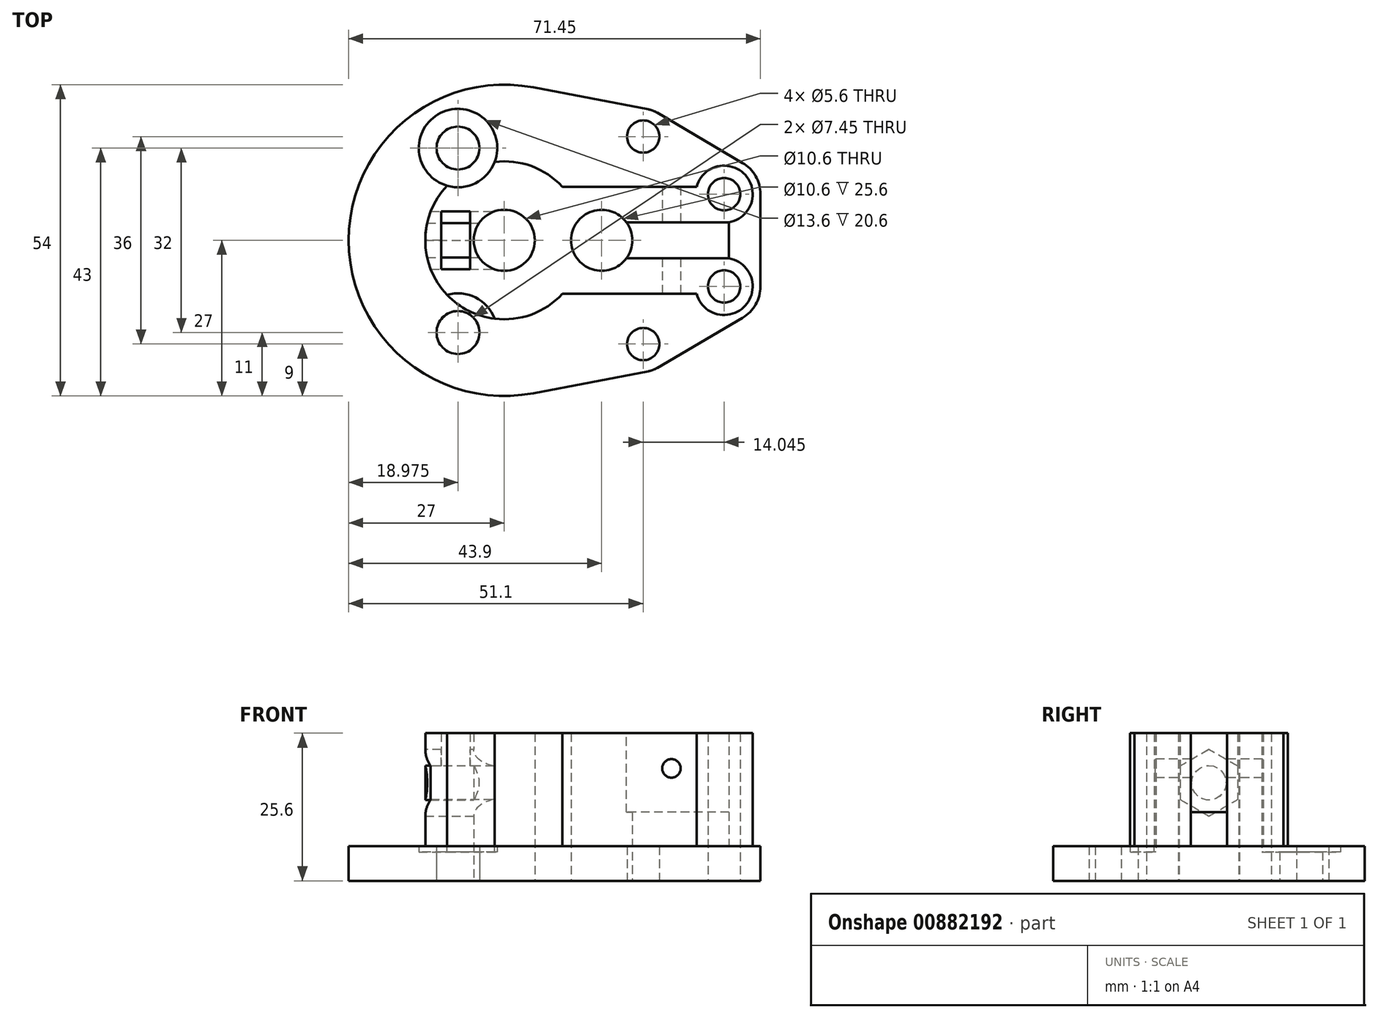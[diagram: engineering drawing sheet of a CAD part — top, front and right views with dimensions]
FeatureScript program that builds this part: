
annotation { "Feature Type Name" : "Feature", "Feature Type Description" : "" }
export const myFeature = defineFeature(function(context is Context, id is Id, definition is map)
    precondition{}
    {
        {
            var Q0;
            Q0=qCreatedBy(makeId("Top.planeOp"),FACE);
            var sketch = newSketch(context, id + "F0", { "sketchPlane" : qUnion([Q0])});
            skCircle(sketch, "E0", {"center": v(0, 0) * mm, "radius": 27 * mm, "construction": true});
            skCircle(sketch, "E1", {"center": v(0, 0) * mm, "radius": 5.3 * mm});
            skCircle(sketch, "E2", {"center": v(16.9, 0) * mm, "radius": 5.3 * mm});
            skCircle(sketch, "E3", {"center": v(-8.03, 16) * mm, "radius": 3.73 * mm});
            skCircle(sketch, "E4", {"center": v(24.1, 18) * mm, "radius": 2.8 * mm});
            skCircle(sketch, "E5", {"center": v(38.15, 8) * mm, "radius": 2.8 * mm});
            skCircle(sketch, "E6.MirrorC", {"center": v(-8.03, -16) * mm, "radius": 3.73 * mm});
            skCircle(sketch, "E7.MirrorC", {"center": v(24.1, -18) * mm, "radius": 2.8 * mm});
            skCircle(sketch, "E8.MirrorC", {"center": v(38.15, -8) * mm, "radius": 2.8 * mm});
            skCircle(sketch, "E9", {"center": v(24.1, 18) * mm, "radius": 4.8 * mm, "construction": true});
            skCircle(sketch, "E10", {"center": v(38.15, 8) * mm, "radius": 6.3 * mm, "construction": true});
            skLineSegment(sketch, "E11", {"start": v(26.53, 22.14) * mm, "end": v(41.34, 13.43) * mm});
            skCircle(sketch, "E12.MirrorC", {"center": v(38.15, -8) * mm, "radius": 6.3 * mm, "construction": true});
            skCircle(sketch, "E13.MirrorC", {"center": v(24.1, -18) * mm, "radius": 4.8 * mm, "construction": true});
            skLineSegment(sketch, "E14", {"start": v(44.45, 8) * mm, "end": v(44.45, -8) * mm});
            skLineSegment(sketch, "E15", {"start": v(41.34, -13.43) * mm, "end": v(26.53, -22.14) * mm});
            skLineSegment(sketch, "E16", {"start": v(5.06, 26.52) * mm, "end": v(25, 22.71) * mm});
            skLineSegment(sketch, "E17", {"start": v(5.06, -26.52) * mm, "end": v(25, -22.71) * mm});
            skArc(sketch, "E18", {"start": v(26.53, 22.14) * mm, "mid": v(25.8, 22.5) * mm, "end": v(25, 22.71) * mm});
            skArc(sketch, "E19", {"start": v(44.45, 8) * mm, "mid": v(43.61, 11.13) * mm, "end": v(41.34, 13.43) * mm});
            skArc(sketch, "E20", {"start": v(41.34, -13.43) * mm, "mid": v(43.61, -11.13) * mm, "end": v(44.44, -8) * mm});
            skArc(sketch, "E21", {"start": v(25, -22.71) * mm, "mid": v(25.8, -22.5) * mm, "end": v(26.53, -22.14) * mm});
            skArc(sketch, "E22", {"start": v(5.06, 26.52) * mm, "mid": v(-27, 0) * mm, "end": v(5.06, -26.52) * mm});
            skSolve(sketch);
        }
        {
            var Q0;
            Q0 = qSketchRegion(id + "F0", true);
            extrude(context, id + "F1", {"entities" : qUnion([Q0]), "depth" : 6 * mm, "offsetDistance" : 25 * mm});
        }
        {
            var Q0;
            Q0=makeQuery(id+"F1.opExtrude","CAP_FACE",FACE,{"disambiguationData":[OSD([sQuery(id+"F0.wireOp",EDGE,"E1"),sQuery(id+"F0.wireOp",EDGE,"E2"),sQuery(id+"F0.wireOp",EDGE,"E3"),sQuery(id+"F0.wireOp",EDGE,"E4"),sQuery(id+"F0.wireOp",EDGE,"E5"),sQuery(id+"F0.wireOp",EDGE,"E6.MirrorC"),sQuery(id+"F0.wireOp",EDGE,"E7.MirrorC"),sQuery(id+"F0.wireOp",EDGE,"E8.MirrorC"),sQuery(id+"F0.wireOp",EDGE,"E11"),sQuery(id+"F0.wireOp",EDGE,"E14"),sQuery(id+"F0.wireOp",EDGE,"E15"),sQuery(id+"F0.wireOp",EDGE,"E16"),sQuery(id+"F0.wireOp",EDGE,"E17"),sQuery(id+"F0.wireOp",EDGE,"E18"),sQuery(id+"F0.wireOp",EDGE,"E19"),sQuery(id+"F0.wireOp",EDGE,"E20"),sQuery(id+"F0.wireOp",EDGE,"E21"),sQuery(id+"F0.wireOp",EDGE,"E22")])],"isStart":false});
            var sketch = newSketch(context, id + "F2", { "sketchPlane" : qUnion([Q0])});
            skCircle(sketch, "E23", {"center": v(0, 0) * mm, "radius": 13.7 * mm});
            skCircle(sketch, "E24", {"center": v(-8.03, 16) * mm, "radius": 6.8 * mm});
            skCircle(sketch, "E25", {"center": v(-8.03, -16) * mm, "radius": 6.8 * mm});
            skCircle(sketch, "E26", {"center": v(38.15, -8) * mm, "radius": 4.95 * mm});
            skCircle(sketch, "E27", {"center": v(38.15, 8) * mm, "radius": 4.95 * mm});
            skLineSegment(sketch, "E28.bottom", {"start": v(0, 9.3) * mm, "end": v(39, 9.3) * mm});
            skLineSegment(sketch, "E28.top", {"start": v(0, -9.3) * mm, "end": v(39, -9.3) * mm});
            skLineSegment(sketch, "E28.left", {"start": v(0, 9.3) * mm, "end": v(0, -9.3) * mm});
            skLineSegment(sketch, "E28.right", {"start": v(39, 9.3) * mm, "end": v(39, -9.3) * mm});
            skSolve(sketch);
        }
        {
            var Q0;
            {var subQ1=sQuery(id+"F2.wireOp",EDGE,"E23");var subQ6=sQuery(id+"F2.wireOp",EDGE,"E28.bottom");var subQ8=makeQuery(id+"F2.imprint","INTERSECT",VERTEX,{"derivedFrom":[subQ1,subQ6]});Q0=makeQuery(id+"F2.imprint","IMPRINT",FACE,{"disambiguationData":[TD([[makeQuery(id+"F2.imprint","IMPRINT",EDGE,{"disambiguationData":[TD([[subQ8,-1.0]])],"derivedFrom":subQ1}),1.0]])]});}
            var Q1;
            {var subQ1=sQuery(id+"F2.wireOp",EDGE,"E28.bottom");var subQ3=sQuery(id+"F2.wireOp",EDGE,"E23");var subQ4=makeQuery(id+"F2.imprint","INTERSECT",VERTEX,{"derivedFrom":[subQ3,subQ1]});Q1=makeQuery(id+"F2.imprint","IMPRINT",FACE,{"disambiguationData":[TD([[makeQuery(id+"F2.imprint","IMPRINT",EDGE,{"disambiguationData":[TD([[subQ4,1.0]])],"derivedFrom":subQ3}),1.0]])]});}
            var Q2;
            {var subQ0=sQuery(id+"F2.wireOp",EDGE,"E28.bottom");var subQ9=sQuery(id+"F2.wireOp",EDGE,"E23");var subQ13=makeQuery(id+"F2.imprint","INTERSECT",VERTEX,{"derivedFrom":[subQ9,subQ0]});Q2=makeQuery(id+"F2.imprint","IMPRINT",FACE,{"disambiguationData":[TD([[makeQuery(id+"F2.imprint","IMPRINT",EDGE,{"disambiguationData":[TD([[subQ13,1.0]])],"derivedFrom":subQ9}),-1.0]])]});}
            var Q3;
            {var subQ0=sQuery(id+"F2.wireOp",EDGE,"E28.top");var subQ1=sQuery(id+"F2.wireOp",EDGE,"E26");var subQ2=makeQuery(id+"F2.imprint","INTERSECT",VERTEX,{"derivedFrom":[subQ1,subQ0]});Q3=makeQuery(id+"F2.imprint","IMPRINT",FACE,{"disambiguationData":[TD([[makeQuery(id+"F2.imprint","IMPRINT",EDGE,{"disambiguationData":[TD([[subQ2,1.0]])],"derivedFrom":subQ1}),1.0]])]});}
            var Q4;
            {var subQ0=sQuery(id+"F2.wireOp",EDGE,"E28.bottom");var subQ1=sQuery(id+"F2.wireOp",EDGE,"E27");var subQ2=makeQuery(id+"F2.imprint","INTERSECT",VERTEX,{"derivedFrom":[subQ1,subQ0]});Q4=makeQuery(id+"F2.imprint","IMPRINT",FACE,{"disambiguationData":[TD([[makeQuery(id+"F2.imprint","IMPRINT",EDGE,{"disambiguationData":[TD([[subQ2,-1.0]])],"derivedFrom":subQ1}),1.0]])]});}
            var Q5;
            {var subQ0=sQuery(id+"F2.wireOp",EDGE,"E28.bottom");var subQ1=sQuery(id+"F2.wireOp",EDGE,"E27");var subQ2=makeQuery(id+"F2.imprint","INTERSECT",VERTEX,{"derivedFrom":[subQ1,subQ0]});Q5=makeQuery(id+"F2.imprint","IMPRINT",FACE,{"disambiguationData":[TD([[makeQuery(id+"F2.imprint","IMPRINT",EDGE,{"disambiguationData":[TD([[subQ2,1.0]])],"derivedFrom":subQ1}),1.0]])]});}
            var Q6;
            {var subQ0=sQuery(id+"F2.wireOp",EDGE,"E28.top");var subQ1=sQuery(id+"F2.wireOp",EDGE,"E26");var subQ2=makeQuery(id+"F2.imprint","INTERSECT",VERTEX,{"derivedFrom":[subQ1,subQ0]});Q6=makeQuery(id+"F2.imprint","IMPRINT",FACE,{"disambiguationData":[TD([[makeQuery(id+"F2.imprint","IMPRINT",EDGE,{"disambiguationData":[TD([[subQ2,-1.0]])],"derivedFrom":subQ1}),1.0]])]});}
            extrude(context, id + "F3", {"entities" : qUnion([Q0, Q1, Q2, Q3, Q4, Q5, Q6]), "operationType" : NewBodyOperationType.ADD, "depth" : 19.6 * mm, "offsetDistance" : 25 * mm});
        }
        {
            var Q0;
            {var subQ0=sQuery(id+"F2.wireOp",EDGE,"E25");var subQ1=sQuery(id+"F2.wireOp",EDGE,"E23");var subQ2=makeQuery(id+"F2.imprint","INTERSECT",VERTEX,{"disambiguationData":[OD(0.0)],"derivedFrom":[subQ1,subQ0]});Q0=makeQuery(id+"F2.imprint","IMPRINT",FACE,{"disambiguationData":[TD([[makeQuery(id+"F2.imprint","IMPRINT",EDGE,{"disambiguationData":[TD([[subQ2,-1.0]])],"derivedFrom":subQ1}),1.0]])]});}
            var Q1;
            Q1=makeQuery(id+"F2.imprint","IMPRINT",FACE,{"disambiguationData":[TD([[makeQuery(id+"F2.imprint","IMPRINT",EDGE,{"derivedFrom":makeQuery(id+"F1.opExtrude","CAP_EDGE",EDGE,{"disambiguationData":[OSD([sQuery(id+"F0.wireOp",EDGE,"E6.MirrorC")])],"isStart":false})}),1.0]])]});
            var Q2;
            Q2=makeQuery(id+"F2.imprint","IMPRINT",FACE,{"disambiguationData":[TD([[makeQuery(id+"F2.imprint","IMPRINT",EDGE,{"derivedFrom":makeQuery(id+"F1.opExtrude","CAP_EDGE",EDGE,{"disambiguationData":[OSD([sQuery(id+"F0.wireOp",EDGE,"E3")])],"isStart":false})}),-1.0]])]});
            var Q3;
            {var subQ0=sQuery(id+"F2.wireOp",EDGE,"E24");var subQ1=sQuery(id+"F2.wireOp",EDGE,"E23");var subQ2=makeQuery(id+"F2.imprint","INTERSECT",VERTEX,{"disambiguationData":[OD(0.0)],"derivedFrom":[subQ1,subQ0]});Q3=makeQuery(id+"F2.imprint","IMPRINT",FACE,{"disambiguationData":[TD([[makeQuery(id+"F2.imprint","IMPRINT",EDGE,{"disambiguationData":[TD([[subQ2,-1.0]])],"derivedFrom":subQ1}),1.0]])]});}
            extrude(context, id + "F4", {"entities" : qUnion([Q0, Q1, Q2, Q3]), "operationType" : NewBodyOperationType.REMOVE, "oppositeDirection" : true, "depth" : 1 * mm, "offsetDistance" : 25 * mm});
        }
        {
            var Q0;
            Q0=makeQuery(id+"F3.opExtrude","CAP_FACE",FACE,{"disambiguationData":[OSD([sQuery(id+"F0.wireOp",EDGE,"E1"),sQuery(id+"F0.wireOp",EDGE,"E2"),sQuery(id+"F0.wireOp",EDGE,"E5"),sQuery(id+"F0.wireOp",EDGE,"E8.MirrorC"),sQuery(id+"F2.wireOp",EDGE,"E23"),sQuery(id+"F2.wireOp",EDGE,"E24"),sQuery(id+"F2.wireOp",EDGE,"E25"),sQuery(id+"F2.wireOp",EDGE,"E26"),sQuery(id+"F2.wireOp",EDGE,"E27"),sQuery(id+"F2.wireOp",EDGE,"E28.bottom"),sQuery(id+"F2.wireOp",EDGE,"E28.top"),sQuery(id+"F2.wireOp",EDGE,"E28.right")])],"isStart":false});
            var sketch = newSketch(context, id + "F5", { "sketchPlane" : qUnion([Q0])});
            skLineSegment(sketch, "E29.bottom", {"start": v(39, -3.12) * mm, "end": v(21.18, -3.12) * mm});
            skLineSegment(sketch, "E29.top", {"start": v(39, 3.12) * mm, "end": v(21.18, 3.12) * mm});
            skLineSegment(sketch, "E29.left", {"start": v(39, -3.12) * mm, "end": v(39, 3.12) * mm});
            skLineSegment(sketch, "E29.right", {"start": v(21.18, -3.12) * mm, "end": v(21.18, 3.12) * mm});
            skLineSegment(sketch, "E30.bottom", {"start": v(-5.95, 5) * mm, "end": v(-10.95, 5) * mm});
            skLineSegment(sketch, "E30.top", {"start": v(-5.95, -5) * mm, "end": v(-10.95, -5) * mm});
            skLineSegment(sketch, "E30.left", {"start": v(-5.95, 5) * mm, "end": v(-5.95, -5) * mm});
            skLineSegment(sketch, "E30.right", {"start": v(-10.95, 5) * mm, "end": v(-10.95, -5) * mm});
            skPoint(sketch, "E30.middle", {"position": v(-8.45, 0) * mm});
            skSolve(sketch);
        }
        {
            var Q0;
            {var subQ0=sQuery(id+"F5.wireOp",EDGE,"E29.bottom");Q0=makeQuery(id+"F5.imprint","IMPRINT",FACE,{"disambiguationData":[TD([[makeQuery(id+"F5.imprint","IMPRINT",EDGE,{"derivedFrom":subQ0}),-1.0]])]});}
            extrude(context, id + "F6", {"entities" : qUnion([Q0]), "operationType" : NewBodyOperationType.REMOVE, "oppositeDirection" : true, "depth" : 13.7 * mm, "offsetDistance" : 25 * mm});
        }
        {
            var Q0;
            Q0=makeQuery(id+"F3.opExtrude","SWEPT_FACE",FACE,{"disambiguationData":[OSD([sQuery(id+"F2.wireOp",EDGE,"E28.top")])]});
            var sketch = newSketch(context, id + "F7", { "sketchPlane" : qUnion([Q0])});
            skCircle(sketch, "E31", {"center": v(29, 19.5) * mm, "radius": 1.6 * mm});
            skSolve(sketch);
        }
        {
            var Q0;
            Q0 = qSketchRegion(id + "F7", true);
            extrude(context, id + "F8", {"entities" : qUnion([Q0]), "operationType" : NewBodyOperationType.REMOVE, "endBound" : BoundingType.THROUGH_ALL, "oppositeDirection" : true, "depth" : 25 * mm, "offsetDistance" : 25 * mm});
        }
        {
            var Q0;
            Q0=sQuery(id+"F5.wireOp",EDGE,"E30.left");
            cPoint(context, id + "F9", {"entities" : qUnion([Q0]), "parameter" : 0.5});
        }
        {
            var Q0;
            Q0=qCreatedBy(makeId("Right.planeOp"),FACE);
            var Q1;
            Q1 = qCreatedBy(id + "F9" ,VERTEX);
            cPlane(context, id + "F10", {"entities" : qUnion([Q0, Q1]), "cplaneType" : CPlaneType.PLANE_POINT, "offset" : 25 * mm, "width" : 150 * mm, "height" : 150 * mm});
        }
        {
            var Q0;
            Q0=qCreatedBy(id+"F10.planeOp",FACE);
            var sketch = newSketch(context, id + "F11", { "sketchPlane" : qUnion([Q0])});
            skLineSegment(sketch, "E32.bottom", {"start": v(-5, 25.6) * mm, "end": v(5, 25.6) * mm});
            skLineSegment(sketch, "E32.top", {"start": v(-5, 17) * mm, "end": v(5, 17) * mm});
            skLineSegment(sketch, "E32.left", {"start": v(-5, 25.6) * mm, "end": v(-5, 17) * mm});
            skLineSegment(sketch, "E32.right", {"start": v(5, 25.6) * mm, "end": v(5, 17) * mm});
            skPoint(sketch, "E32.middle", {"position": v(0, 21.3) * mm});
            skCircle(sketch, "E33", {"center": v(0, 17) * mm, "radius": 3 * mm});
            skCircle(sketch, "E34.cCircle", {"center": v(0, 17) * mm, "radius": 5 * mm, "construction": true});
            skLineSegment(sketch, "E34.0", {"start": v(-5, 14.11) * mm, "end": v(-5, 19.89) * mm});
            skLineSegment(sketch, "E34.1", {"start": v(-5, 19.89) * mm, "end": v(0, 22.77) * mm});
            skLineSegment(sketch, "E34.2", {"start": v(0, 22.77) * mm, "end": v(5, 19.89) * mm});
            skLineSegment(sketch, "E34.3", {"start": v(5, 19.89) * mm, "end": v(5, 14.11) * mm});
            skLineSegment(sketch, "E34.4", {"start": v(5, 14.11) * mm, "end": v(0, 11.23) * mm});
            skLineSegment(sketch, "E34.5", {"start": v(0, 11.23) * mm, "end": v(-5, 14.11) * mm});
            skPoint(sketch, "E34.0.midPoint", {"position": v(-5, 17) * mm});
            skSolve(sketch);
        }
        {
            var Q0;
            Q0 = qSketchRegion(id + "F11", true);
            var Q1;
            {var subQ0=sQuery(id+"F11.wireOp",EDGE,"E33");var subQ1=sQuery(id+"F11.wireOp",EDGE,"E32.top");var subQ2=makeQuery(id+"F11.imprint","INTERSECT",VERTEX,{"disambiguationData":[OD(0.0)],"derivedFrom":[subQ1,subQ0]});Q1=makeQuery(id+"F11.imprint","IMPRINT",FACE,{"disambiguationData":[TD([[makeQuery(id+"F11.imprint","IMPRINT",EDGE,{"disambiguationData":[TD([[subQ2,-1.0]])],"derivedFrom":subQ1}),-1.0]])]});}
            var Q2;
            {var subQ0=sQuery(id+"F11.wireOp",EDGE,"E33");var subQ1=sQuery(id+"F11.wireOp",EDGE,"E32.top");var subQ2=makeQuery(id+"F11.imprint","INTERSECT",VERTEX,{"disambiguationData":[OD(0.0)],"derivedFrom":[subQ1,subQ0]});Q2=makeQuery(id+"F11.imprint","IMPRINT",FACE,{"disambiguationData":[TD([[makeQuery(id+"F11.imprint","IMPRINT",EDGE,{"disambiguationData":[TD([[subQ2,-1.0]])],"derivedFrom":subQ1}),1.0]])]});}
            extrude(context, id + "F12", {"entities" : qUnion([Q0, Q1, Q2]), "operationType" : NewBodyOperationType.REMOVE, "oppositeDirection" : true, "depth" : 5 * mm, "offsetDistance" : 25 * mm});
        }
        {
            var Q0;
            {var subQ0=sQuery(id+"F11.wireOp",EDGE,"E33");var subQ1=sQuery(id+"F11.wireOp",EDGE,"E32.top");var subQ2=makeQuery(id+"F11.imprint","INTERSECT",VERTEX,{"disambiguationData":[OD(0.0)],"derivedFrom":[subQ1,subQ0]});Q0=makeQuery(id+"F11.imprint","IMPRINT",FACE,{"disambiguationData":[TD([[makeQuery(id+"F11.imprint","IMPRINT",EDGE,{"disambiguationData":[TD([[subQ2,-1.0]])],"derivedFrom":subQ1}),1.0]])]});}
            var Q1;
            {var subQ0=sQuery(id+"F11.wireOp",EDGE,"E33");var subQ1=sQuery(id+"F11.wireOp",EDGE,"E32.top");var subQ2=makeQuery(id+"F11.imprint","INTERSECT",VERTEX,{"disambiguationData":[OD(0.0)],"derivedFrom":[subQ1,subQ0]});Q1=makeQuery(id+"F11.imprint","IMPRINT",FACE,{"disambiguationData":[TD([[makeQuery(id+"F11.imprint","IMPRINT",EDGE,{"disambiguationData":[TD([[subQ2,-1.0]])],"derivedFrom":subQ1}),-1.0]])]});}
            extrude(context, id + "F13", {"entities" : qUnion([Q0, Q1]), "operationType" : NewBodyOperationType.REMOVE, "depth" : 5 * mm, "offsetDistance" : 25 * mm, "hasSecondDirection" : true, "secondDirectionOppositeDirection" : true, "secondDirectionDepth" : 10 * mm});
        }
        {
            var Q0;
            Q0=qCreatedBy(makeId("Front.planeOp"),FACE);
            var sketch = newSketch(context, id + "F14", { "sketchPlane" : qUnion([Q0])});
            skLineSegment(sketch, "E35", {"start": v(0, 0) * mm, "end": v(0, 28.67) * mm, "construction": true});
            skSolve(sketch);
        }
    });
